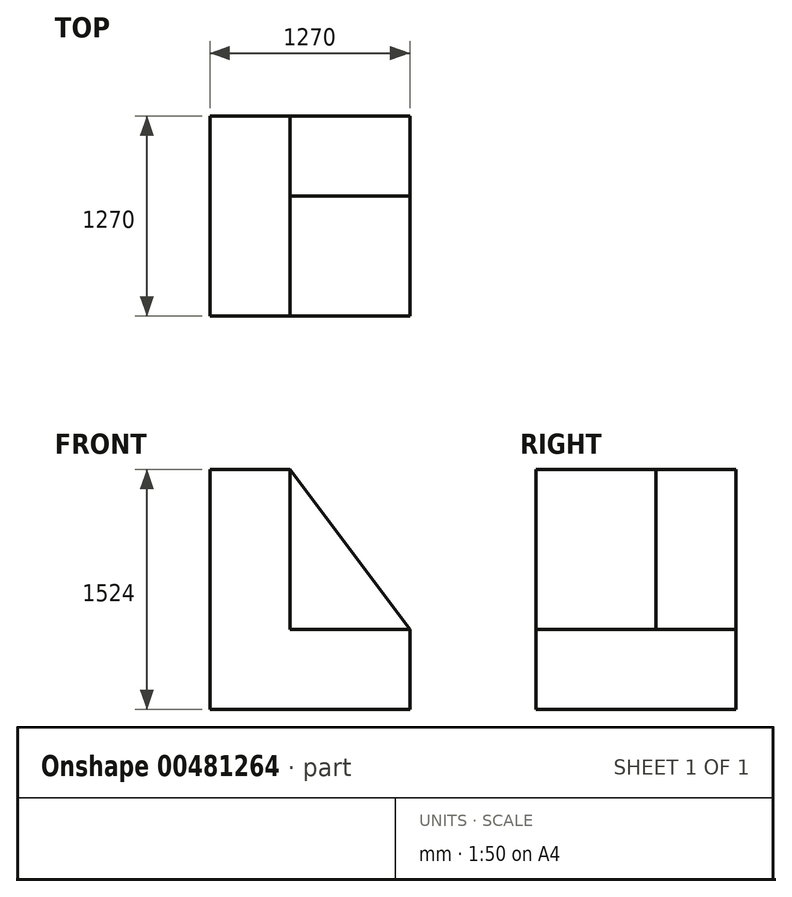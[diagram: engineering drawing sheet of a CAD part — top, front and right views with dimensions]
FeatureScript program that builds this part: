
annotation { "Feature Type Name" : "Feature", "Feature Type Description" : "" }
export const myFeature = defineFeature(function(context is Context, id is Id, definition is map)
    precondition{}
    {
        {
            var Q0;
            Q0=qCreatedBy(makeId("Front.planeOp"),FACE);
            var sketch = newSketch(context, id + "F0", { "sketchPlane" : qUnion([Q0])});
            skLineSegment(sketch, "E0", {"start": v(0, 0) * mm, "end": v(1270, 0) * mm});
            skLineSegment(sketch, "E1", {"start": v(1270, 0) * mm, "end": v(1270, 508) * mm});
            skLineSegment(sketch, "E2", {"start": v(1270, 508) * mm, "end": v(508, 508) * mm});
            skLineSegment(sketch, "E3", {"start": v(508, 508) * mm, "end": v(508, 1524) * mm});
            skLineSegment(sketch, "E4", {"start": v(508, 1524) * mm, "end": v(0, 1524) * mm});
            skLineSegment(sketch, "E5", {"start": v(0, 1524) * mm, "end": v(0, 0) * mm});
            skSolve(sketch);
        }
        {
            var Q0;
            Q0=makeQuery(id+"F0.imprint","IMPRINT",FACE,{"disambiguationData":[TD([[makeQuery(id+"F0.imprint","IMPRINT",EDGE,{"derivedFrom":sQuery(id+"F0.wireOp",EDGE,"E0")}),1.0]])]});
            extrude(context, id + "F1", {"entities" : qUnion([Q0]), "depth" : 1270 * mm});
        }
        {
            var Q0;
            Q0=makeQuery(id+"F1.opExtrude","CAP_FACE",FACE,{"disambiguationData":[OSD([sQuery(id+"F0.wireOp",EDGE,"E0"),sQuery(id+"F0.wireOp",EDGE,"E1"),sQuery(id+"F0.wireOp",EDGE,"E2"),sQuery(id+"F0.wireOp",EDGE,"E3"),sQuery(id+"F0.wireOp",EDGE,"E4"),sQuery(id+"F0.wireOp",EDGE,"E5")])],"isStart":true});
            var sketch = newSketch(context, id + "F2", { "sketchPlane" : qUnion([Q0])});
            skLineSegment(sketch, "E6", {"start": v(-508, 1524) * mm, "end": v(-1270, 508) * mm});
            skLineSegment(sketch, "E7", {"start": v(-1270, 508) * mm, "end": v(-508, 508) * mm});
            skLineSegment(sketch, "E8", {"start": v(-508, 508) * mm, "end": v(-508, 1524) * mm});
            skSolve(sketch);
        }
        {
            var Q0;
            Q0=makeQuery(id+"F2.imprint","IMPRINT",FACE,{"disambiguationData":[TD([[makeQuery(id+"F2.imprint","IMPRINT",EDGE,{"derivedFrom":sQuery(id+"F2.wireOp",EDGE,"E6")}),1.0]])]});
            extrude(context, id + "F3", {"entities" : qUnion([Q0]), "operationType" : NewBodyOperationType.ADD, "oppositeDirection" : true, "depth" : 508 * mm});
        }
    });
